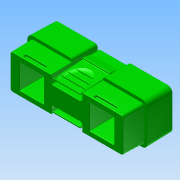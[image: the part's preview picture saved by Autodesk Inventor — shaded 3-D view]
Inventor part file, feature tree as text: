
AUTODESK INVENTOR PART (.ipt)
format: ipt  version: 2014 (Build 180170000, 170)  size: 1,798,144 bytes
history: native  units: in
note: dims shown in document units (in); Inventor stores cm internally (conversion verified against a paired STEP export)
features: extrude x8, fillet x8, sketch x7, draft x4, mirror x2, projected_geometry x1
ambient origin geometry x8: Origin, YZ Plane, XZ Plane, XY Plane, X Axis, Y Axis, Z Axis, Center Point
bodies: Solid1 (feature_tree)
feature tree (30):
  sketch  "Sketch1"  dims[d0=0.34in d1=0.8in]
  extrude  "Extrusion1"  Depth=0.8in
  extrude  "Extrusion2"  Depth=0.2975in
  extrude  "Extrusion3"  Depth=0.06in
  draft  "FaceDraft1"
  draft  "FaceDraft2"
  extrude  "Extrusion4"  Depth=0.5in TaperAngle=0.0deg
  extrude  "Extrusion5"  Depth=0.15in
  fillet  "Fillet1"  Radius=0.33in
  fillet  "Fillet2"  Radius=0.0069in
  extrude  "Extrusion6"  Depth=0.17in
  draft  "FaceDraft3"
  fillet  "Fillet3"  Radius=0.17in
  fillet  "Fillet4"  Radius=0.04in
  fillet  "Fillet5"  Radius=0.09in
  extrude  "Extrusion7"  Depth=0.03in
  extrude  "Extrusion8"  Depth=0.33in
  draft  "FaceDraft4"
  fillet  "Fillet6"  Radius=0.0206in
  fillet  "Fillet7"  Radius=0.0412in
  fillet  "Fillet8"  Radius=0.2625in
  mirror  "Mirror1"
  mirror  "Mirror2"
  sketch  "Sketch2"  dims[d2=0.175in d3=0.2975in]
  sketch  "Sketch3"  dims[d4=0.06in d5=0.06in]
  sketch  "Sketch4"  dims[d6=0.4in d7=0.0in d8=0.5in d9=0.0in]
  projected_geometry  "Projected Loop1"
  sketch  "Sketch5"  dims[d11=0.8in d12=0.15in d13=0.33in d14=0.0in d15=0.0069in]
  sketch  "Sketch6"  dims[d16=0.0069in d17=0.17in d18=0.17in d19=0.04in d20=0.09in]
  sketch  "Sketch7"  dims[d21=0.84in d22=0.03in d24=0.33in d25=0.0206in d26=0.0412in d27=0.2625in d28=0.0in d31=0.25in d32=0.1in d33=0.2in d34=0.6174in d35=0.01in d36=0.02in d37=0.0in d38=0.05in d39=0.185in d40=0.02in d41=0.125in d42=0.24in d43=0.36in d44=0.26in d45=0.01in d46=0.01in d47=0.0in d48=0.0137in d49=0.4in d50=0.06in d51=0.48in d52=0.3in d53=0.04in d54=0.0in d55=0.2375in d56=0.47in d57=0.186in d58=0.47in d59=0.0in d60=0.0069in d61=0.05in d62=0.01in d63=0.005in d64=0.1in]
